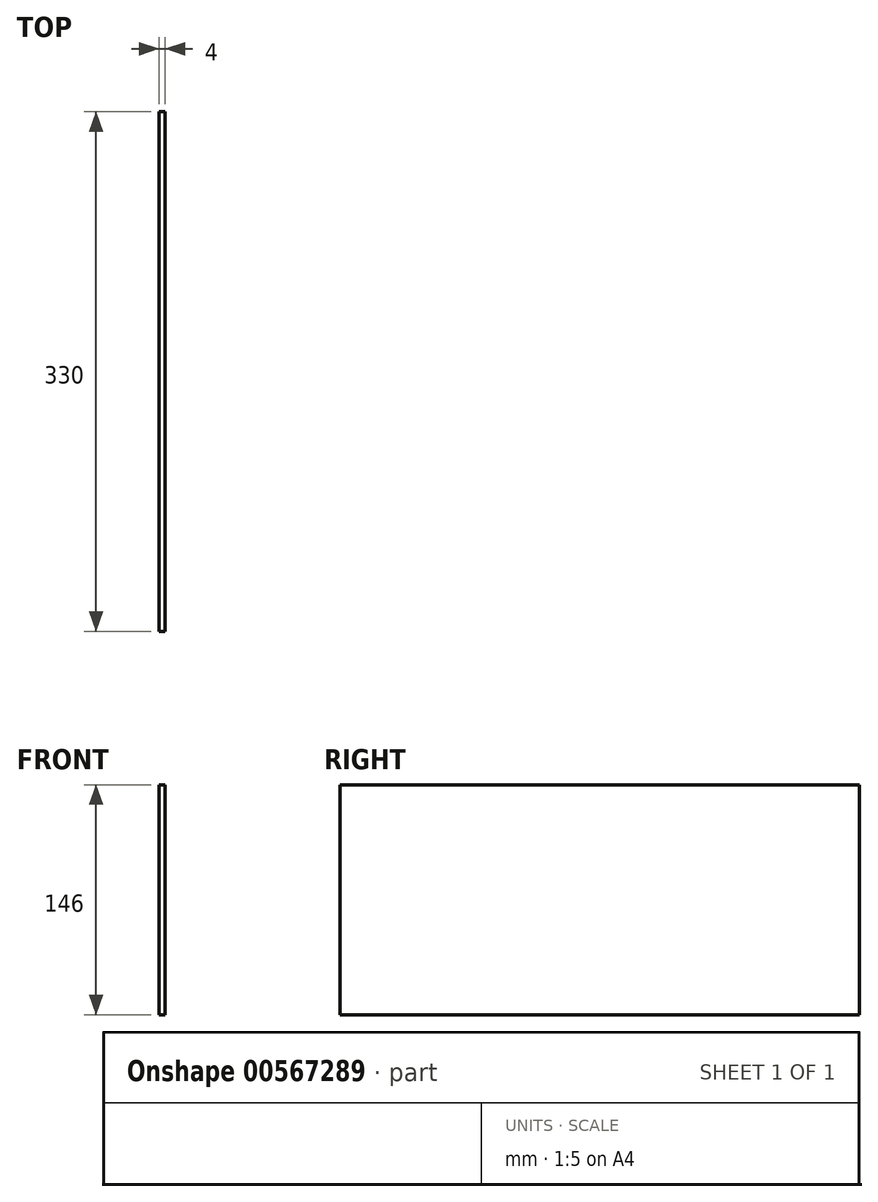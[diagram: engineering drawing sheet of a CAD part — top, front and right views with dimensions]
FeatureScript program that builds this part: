
annotation { "Feature Type Name" : "Feature", "Feature Type Description" : "" }
export const myFeature = defineFeature(function(context is Context, id is Id, definition is map)
    precondition{}
    {
        {
            var Q0;
            Q0=qCreatedBy(makeId("Right.planeOp"),FACE);
            var sketch = newSketch(context, id + "F0", { "sketchPlane" : qUnion([Q0])});
            skLineSegment(sketch, "E0.bottom", {"start": v(-204.05, 9.2) * mm, "end": v(125.95, 9.2) * mm});
            skLineSegment(sketch, "E0.top", {"start": v(-204.05, -136.8) * mm, "end": v(125.95, -136.8) * mm});
            skLineSegment(sketch, "E0.left", {"start": v(-204.05, 9.2) * mm, "end": v(-204.05, -136.8) * mm});
            skLineSegment(sketch, "E0.right", {"start": v(125.95, 9.2) * mm, "end": v(125.95, -136.8) * mm});
            skSolve(sketch);
        }
        {
            var Q0;
            Q0 = qSketchRegion(id + "F0", true);
            extrude(context, id + "F1", {"entities" : qUnion([Q0]), "depth" : 4 * mm, "offsetDistance" : 25 * mm});
        }
    });
